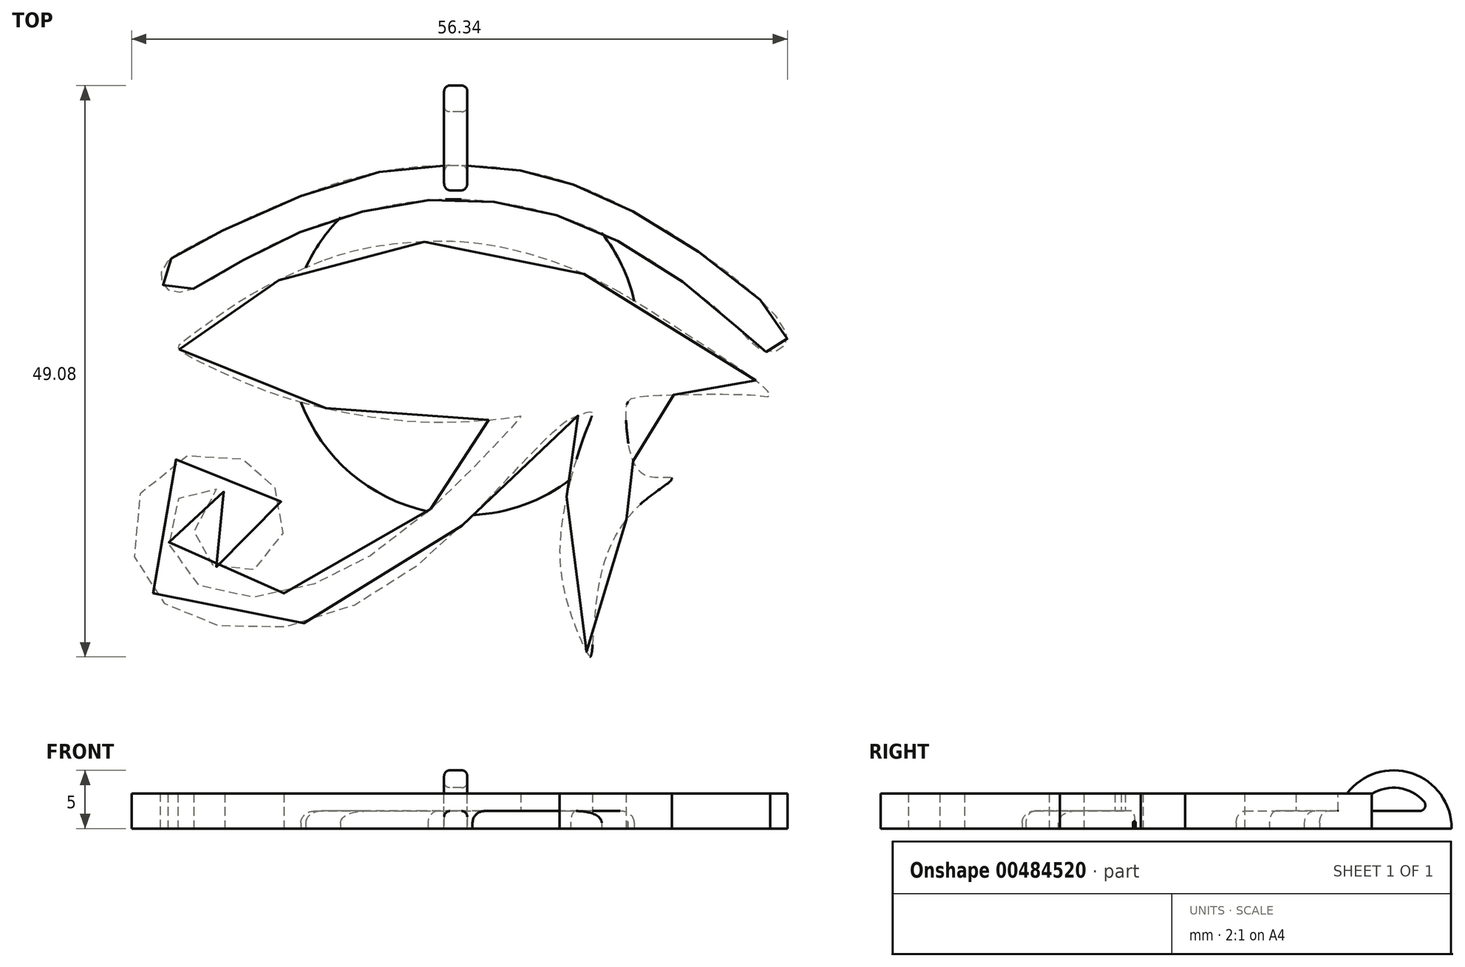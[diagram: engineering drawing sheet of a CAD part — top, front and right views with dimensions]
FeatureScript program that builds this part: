
annotation { "Feature Type Name" : "Feature", "Feature Type Description" : "" }
export const myFeature = defineFeature(function(context is Context, id is Id, definition is map)
    precondition{}
    {
        {
            var Q0;
            Q0=qCreatedBy(makeId("Top.planeOp"),FACE);
            var sketch = newSketch(context, id + "F0", { "sketchPlane" : qUnion([Q0])});
            skFitSpline(sketch, "E0", {"points": [v(0, 14.25) * mm, v(-9.02, 13.09) * mm, v(-21.95, 7.72) * mm, v(-25.22, 5.34) * mm, v(-25.1, 3.9) * mm, v(-23.47, 3.39) * mm, v(-18.23, 6.13) * mm, v(-10.6, 9.55) * mm, v(-1.57, 11.32) * mm, v(6.84, 10.46) * mm, v(15.32, 6.99) * mm, v(23.99, 0.52) * mm, v(26.55, -1.74) * mm, v(28.14, -1.37) * mm, v(28.38, 0) * mm, v(21.97, 6.07) * mm, v(12.15, 11.8) * mm, v(5.87, 13.76) * mm, v(0, 14.25) * mm]});
            skFitSpline(sketch, "E1", {"points": [v(-2.69, 7.68) * mm, v(-8.86, 6.86) * mm, v(-14.47, 4.75) * mm, v(-18.95, 2.29) * mm, v(-23.7, -1.12) * mm, v(-23.87, -1.34) * mm, v(-23.65, -1.64) * mm, v(-17.7, -4.57) * mm, v(-11.23, -6.6) * mm, v(-3.94, -7.72) * mm, v(2.75, -7.63) * mm, v(5.5, -7.29) * mm, v(5.6, -7.29) * mm, v(-1.78, -14.92) * mm, v(-8.73, -20.1) * mm, v(-14.98, -22.56) * mm, v(-20.76, -22.43) * mm, v(-24.14, -19.69) * mm, v(-24.44, -15.36) * mm, v(-22.36, -13.54) * mm, v(-20.12, -13.63) * mm, v(-19.86, -13.72) * mm, v(-20.16, -13.89) * mm, v(-22.14, -15.27) * mm, v(-22.27, -18.2) * mm, v(-20.9, -20.06) * mm, v(-17.92, -20.66) * mm, v(-15.16, -18.42) * mm, v(-15.03, -14.58) * mm, v(-16.7, -12.03) * mm, v(-20.07, -10.54) * mm, v(-25.84, -12.14) * mm, v(-27.8, -18.37) * mm, v(-25.4, -23.08) * mm, v(-20.16, -25.32) * mm, v(-12.44, -24.93) * mm, v(-4.2, -20.79) * mm, v(2.88, -14.32) * mm, v(9.09, -8.02) * mm, v(10.38, -7.29) * mm, v(11.67, -6.94) * mm, v(11.63, -7.46) * mm, v(10.64, -10.14) * mm, v(9.3, -15.35) * mm, v(9.26, -22.04) * mm, v(11.37, -27.78) * mm, v(11.59, -27.95) * mm, v(12.4, -21.3) * mm, v(15.9, -14.84) * mm, v(18.53, -12.77) * mm, v(18.53, -12.6) * mm, v(16.2, -12.34) * mm, v(14.7, -8.45) * mm, v(14.78, -6.08) * mm, v(15.38, -5.7) * mm, v(19.78, -5.43) * mm, v(26, -5.52) * mm, v(26.99, -5.56) * mm, v(26.77, -5.09) * mm, v(20.04, -0.39) * mm, v(10.64, 5.1) * mm, v(2.44, 7.46) * mm, v(-2.69, 7.68) * mm]});
            skFitSpline(sketch, "E2", {"points": [v(-8.25, 4.06) * mm, v(-15.41, 1.2) * mm, v(-18.18, -0.69) * mm, v(-18.18, -0.86) * mm, v(-12.96, -3.06) * mm, v(-5.62, -4.57) * mm, v(-1.44, -4.7) * mm, v(-1.44, -4.7) * mm, v(-3.68, -3.7) * mm, v(-5.92, -0.52) * mm, v(-5.15, 3.02) * mm, v(-3.42, 4.79) * mm, v(-3.42, 4.79) * mm, v(-8.25, 4.06) * mm]});
            skFitSpline(sketch, "E3", {"points": [v(7.6, 3.35) * mm, v(4.94, 4.25) * mm, v(4.94, 4.25) * mm, v(6.13, 1.99) * mm, v(6.22, -1.3) * mm, v(4.36, -3.57) * mm, v(3.44, -4.19) * mm, v(3.44, -4.19) * mm, v(8.1, -3.93) * mm, v(13.62, -3.1) * mm, v(17.79, -2.53) * mm, v(17.8, -2.52) * mm, v(7.6, 3.35) * mm]});
            skSolve(sketch);
        }
        {
            var Q0;
            Q0=qCreatedBy(makeId("Top.planeOp"),FACE);
            var sketch = newSketch(context, id + "F1", { "sketchPlane" : qUnion([Q0])});
            skCircle(sketch, "E4", {"center": v(0.74, -0.8) * mm, "radius": 15 * mm});
            skSolve(sketch);
        }
        {
            var Q0;
            Q0 = qSketchRegion(id + "F1", true);
            extrude(context, id + "F2", {"entities" : qUnion([Q0]), "depth" : 1.5 * mm});
        }
        {
            var Q0;
            Q0 = qSketchRegion(id + "F0", true);
            extrude(context, id + "F3", {"entities" : qUnion([Q0]), "operationType" : NewBodyOperationType.ADD, "depth" : 3 * mm});
        }
        {
            var Q0;
            {var subQ0=sQuery(id+"F1.wireOp",EDGE,"E4");Q0=makeQuery(id+"F3.boolean.opBoolean","SPLIT",EDGE,{"disambiguationData":[TD([makeQuery(id+"F2.opExtrude","SWEPT_FACE",FACE,{"disambiguationData":[OSD([subQ0])]}),makeQuery(id+"F2.opExtrude","CAP_FACE",FACE,{"disambiguationData":[OSD([subQ0])],"isStart":false}),makeQuery(id+"F3.opExtrude","SWEPT_FACE",FACE,{"disambiguationData":[OSD([sQuery(id+"F0.wireOp",EDGE,"E1")])]})]),OD(0.0)],"derivedFrom":makeQuery(id+"F2.opExtrude","CAP_EDGE",EDGE,{"disambiguationData":[OSD([subQ0])],"isStart":false})});}
            var Q1;
            {var subQ0=sQuery(id+"F1.wireOp",EDGE,"E4");Q1=makeQuery(id+"F3.boolean.opBoolean","SPLIT",EDGE,{"disambiguationData":[TD([makeQuery(id+"F2.opExtrude","SWEPT_FACE",FACE,{"disambiguationData":[OSD([subQ0])]}),makeQuery(id+"F2.opExtrude","CAP_FACE",FACE,{"disambiguationData":[OSD([subQ0])],"isStart":false}),makeQuery(id+"F3.opExtrude","SWEPT_FACE",FACE,{"disambiguationData":[OSD([sQuery(id+"F0.wireOp",EDGE,"E1")])]})]),OD(1.0)],"derivedFrom":makeQuery(id+"F2.opExtrude","CAP_EDGE",EDGE,{"disambiguationData":[OSD([subQ0])],"isStart":false})});}
            var Q2;
            {var subQ0=sQuery(id+"F1.wireOp",EDGE,"E4");Q2=makeQuery(id+"F3.boolean.opBoolean","SPLIT",EDGE,{"disambiguationData":[TD([makeQuery(id+"F2.opExtrude","SWEPT_FACE",FACE,{"disambiguationData":[OSD([subQ0])]}),makeQuery(id+"F2.opExtrude","CAP_FACE",FACE,{"disambiguationData":[OSD([subQ0])],"isStart":false}),makeQuery(id+"F3.opExtrude","SWEPT_FACE",FACE,{"disambiguationData":[OSD([sQuery(id+"F0.wireOp",EDGE,"E3")])]})])],"derivedFrom":makeQuery(id+"F2.opExtrude","CAP_EDGE",EDGE,{"disambiguationData":[OSD([subQ0])],"isStart":false})});}
            var Q3;
            {var subQ0=sQuery(id+"F1.wireOp",EDGE,"E4");Q3=makeQuery(id+"F3.boolean.opBoolean","SPLIT",EDGE,{"disambiguationData":[TD([makeQuery(id+"F2.opExtrude","SWEPT_FACE",FACE,{"disambiguationData":[OSD([subQ0])]}),makeQuery(id+"F2.opExtrude","CAP_FACE",FACE,{"disambiguationData":[OSD([subQ0])],"isStart":false}),makeQuery(id+"F3.opExtrude","SWEPT_FACE",FACE,{"disambiguationData":[OSD([sQuery(id+"F0.wireOp",EDGE,"E0")])]}),makeQuery(id+"F3.opExtrude","SWEPT_FACE",FACE,{"disambiguationData":[OSD([sQuery(id+"F0.wireOp",EDGE,"E1")])]})]),OD(1.0)],"derivedFrom":makeQuery(id+"F2.opExtrude","CAP_EDGE",EDGE,{"disambiguationData":[OSD([subQ0])],"isStart":false})});}
            var Q4;
            {var subQ0=sQuery(id+"F1.wireOp",EDGE,"E4");Q4=makeQuery(id+"F3.boolean.opBoolean","SPLIT",EDGE,{"disambiguationData":[TD([makeQuery(id+"F2.opExtrude","SWEPT_FACE",FACE,{"disambiguationData":[OSD([subQ0])]}),makeQuery(id+"F2.opExtrude","CAP_FACE",FACE,{"disambiguationData":[OSD([subQ0])],"isStart":false}),makeQuery(id+"F3.opExtrude","SWEPT_FACE",FACE,{"disambiguationData":[OSD([sQuery(id+"F0.wireOp",EDGE,"E0")])]}),makeQuery(id+"F3.opExtrude","SWEPT_FACE",FACE,{"disambiguationData":[OSD([sQuery(id+"F0.wireOp",EDGE,"E1")])]})]),OD(0.0)],"derivedFrom":makeQuery(id+"F2.opExtrude","CAP_EDGE",EDGE,{"disambiguationData":[OSD([subQ0])],"isStart":false})});}
            var Q5;
            {var subQ0=sQuery(id+"F1.wireOp",EDGE,"E4");Q5=makeQuery(id+"F3.boolean.opBoolean","SPLIT",EDGE,{"disambiguationData":[TD([makeQuery(id+"F2.opExtrude","SWEPT_FACE",FACE,{"disambiguationData":[OSD([subQ0])]}),makeQuery(id+"F2.opExtrude","CAP_FACE",FACE,{"disambiguationData":[OSD([subQ0])],"isStart":false}),makeQuery(id+"F3.opExtrude","SWEPT_FACE",FACE,{"disambiguationData":[OSD([sQuery(id+"F0.wireOp",EDGE,"E2")])]})])],"derivedFrom":makeQuery(id+"F2.opExtrude","CAP_EDGE",EDGE,{"disambiguationData":[OSD([subQ0])],"isStart":false})});}
            fillet(context, id + "F4", {"entities" : qUnion([Q0, Q1, Q2, Q3, Q4, Q5]), "radius" : 1 * mm, "tangentPropagation" : true, "allowEdgeOverflow" : false});
        }
        {
            var Q0;
            Q0=qCreatedBy(makeId("Right.planeOp"),FACE);
            var sketch = newSketch(context, id + "F5", { "sketchPlane" : qUnion([Q0])});
            skLineSegment(sketch, "E5.0", {"start": v(14.25, 0) * mm, "end": v(-1.8, 0) * mm, "construction": true});
            skLineSegment(sketch, "E6", {"start": v(14.25, 0) * mm, "end": v(21.11, 0) * mm});
            skArc(sketch, "E7", {"start": v(21.11, 0) * mm, "mid": v(16.11, 5) * mm, "end": v(11.11, 0) * mm});
            skLineSegment(sketch, "E8", {"start": v(14.25, 0) * mm, "end": v(11.11, 0) * mm});
            skArc(sketch, "E9", {"start": v(19.28, 1.5) * mm, "mid": v(16.11, 3.5) * mm, "end": v(12.95, 1.5) * mm});
            skLineSegment(sketch, "E10", {"start": v(19.28, 1.5) * mm, "end": v(12.95, 1.5) * mm});
            skSolve(sketch);
        }
        {
            var Q0;
            Q0 = qSketchRegion(id + "F5", true);
            extrude(context, id + "F6", {"entities" : qUnion([Q0]), "operationType" : NewBodyOperationType.ADD, "endBound" : BoundingType.SYMMETRIC, "depth" : 2 * mm});
        }
        {
            var Q0;
            Q0=makeQuery(id+"F6.opExtrude","CAP_EDGE",EDGE,{"disambiguationData":[OSD([sQuery(id+"F5.wireOp",EDGE,"E7")])],"isStart":true});
            var Q1;
            Q1=makeQuery(id+"F6.opExtrude","CAP_EDGE",EDGE,{"disambiguationData":[OSD([sQuery(id+"F5.wireOp",EDGE,"E7")])],"isStart":false});
            var Q2;
            Q2=makeQuery(id+"F6.opExtrude","CAP_EDGE",EDGE,{"disambiguationData":[OSD([sQuery(id+"F5.wireOp",EDGE,"E10")])],"isStart":true});
            var Q3;
            Q3=makeQuery(id+"F6.opExtrude","CAP_EDGE",EDGE,{"disambiguationData":[OSD([sQuery(id+"F5.wireOp",EDGE,"E10")])],"isStart":false});
            var Q4;
            Q4=makeQuery(id+"F6.opExtrude","CAP_EDGE",EDGE,{"disambiguationData":[OSD([sQuery(id+"F5.wireOp",EDGE,"E9")])],"isStart":true});
            var Q5;
            Q5=makeQuery(id+"F6.opExtrude","CAP_EDGE",EDGE,{"disambiguationData":[OSD([sQuery(id+"F5.wireOp",EDGE,"E9")])],"isStart":false});
            var Q6;
            {var subQ0=sQuery(id+"F5.wireOp",EDGE,"E10");var subQ1=sQuery(id+"F5.wireOp",EDGE,"E9");Q6=makeQuery(id+"F6.opExtrude","SWEPT_EDGE",EDGE,{"disambiguationData":[OSD([subQ1,subQ0]),TDD([makeQuery(id+"F5.imprint","INTERSECT",VERTEX,{"disambiguationData":[OD(0.0)],"derivedFrom":[subQ1,subQ0]})])]});}
            fillet(context, id + "F7", {"entities" : qUnion([Q0, Q1, Q2, Q3, Q4, Q5, Q6]), "radius" : .5 * mm, "tangentPropagation" : true, "allowEdgeOverflow" : false});
        }
    });
